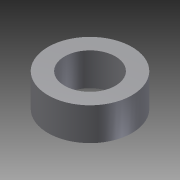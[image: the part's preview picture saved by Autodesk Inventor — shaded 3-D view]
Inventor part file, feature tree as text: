
AUTODESK INVENTOR PART (.ipt)
format: ipt  version: 2014 SP2 (Build 180246200, 246)  size: 97,280 bytes
history: native  units: in
note: dims shown in document units (in); Inventor stores cm internally (conversion verified against a paired STEP export)
features: extrude x2, sketch x2, other x1, imported_body x1
ambient origin geometry x8: Origin, YZ Plane, XZ Plane, XY Plane, X Axis, Y Axis, Z Axis, Center Point
bodies: Body1 (feature_tree)
feature tree (6):
  parser-record x1  (decoder bookkeeping rows leaked as tree rows — omitted from the tree; the rows remain in map.json)
  imported_body  "Base1"
  extrude  "Extrusion1"  Depth=1.0in TaperAngle=0.0deg
  extrude  "Extrusion2"  [1 undecoded]
  sketch  "Sketch1"  dims[d0=0.32in d1=1.0in d2=0.0in]
  sketch  "Sketch2"  dims[d3=0.125in d4=0.0in]
note: 1 required parameter value undecoded (feature->parameter linkage not recoverable at this tier; creation-order binding heuristic only, values carry confidence <= 0.55)
